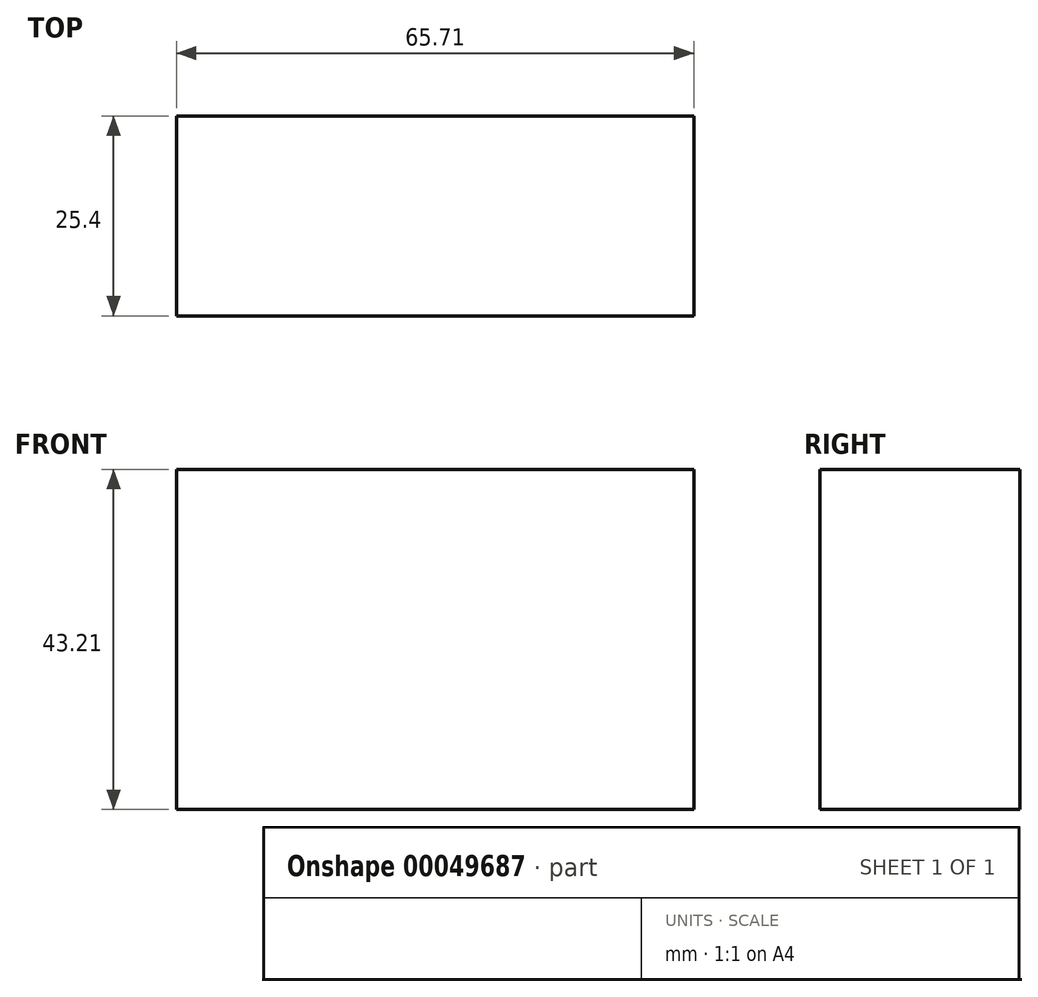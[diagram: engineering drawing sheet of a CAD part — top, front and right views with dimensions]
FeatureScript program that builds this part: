
annotation { "Feature Type Name" : "Feature", "Feature Type Description" : "" }
export const myFeature = defineFeature(function(context is Context, id is Id, definition is map)
    precondition{}
    {
        {
            var Q0;
            Q0=qCreatedBy(makeId("Front.planeOp"),FACE);
            var sketch = newSketch(context, id + "F0", { "sketchPlane" : qUnion([Q0])});
            skLineSegment(sketch, "E0.bottom", {"start": v(-151.27, 35.05) * mm, "end": v(-85.56, 35.05) * mm});
            skLineSegment(sketch, "E0.top", {"start": v(-151.27, -8.16) * mm, "end": v(-85.56, -8.16) * mm});
            skLineSegment(sketch, "E0.left", {"start": v(-151.27, 35.05) * mm, "end": v(-151.27, -8.16) * mm});
            skLineSegment(sketch, "E0.right", {"start": v(-85.56, 35.05) * mm, "end": v(-85.56, -8.16) * mm});
            skSolve(sketch);
        }
        {
            var Q0;
            Q0 = qSketchRegion(id + "F0", true);
            extrude(context, id + "F1", {"entities" : qUnion([Q0]), "depth" : 25.4 * mm});
        }
    });
